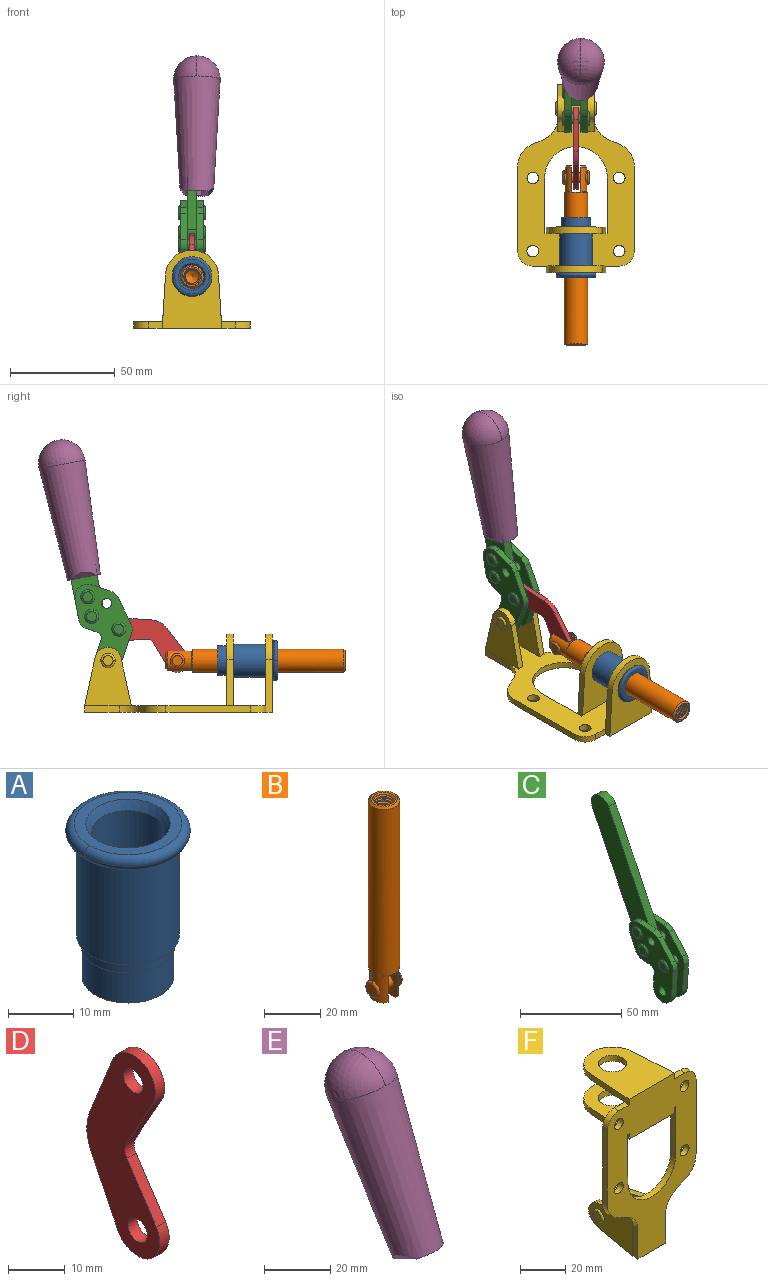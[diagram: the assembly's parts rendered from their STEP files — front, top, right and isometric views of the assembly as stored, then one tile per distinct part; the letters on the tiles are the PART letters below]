
ASSEMBLY  parts=6 mates=6
PART A: 15 faces, bbox 20.6x20.6x28.7 mm
  f0: torus R=8.26mm, axis (0,0,1), area 56.8mm2, adj f1,f10,f12
  f1: torus R=8.26mm, axis (0,0,1), area 56.8mm2, adj f0,f6,f13
  f2: cylinder r=5.59mm len=25.91mm, axis (0,0,1), area 909.6mm2, adj f3,f4
  f3: cone r=6.86mm half-angle=45deg, axis (0,0,-1), area 70.2mm2, adj f2,f14
  f4: cone r=6.47mm half-angle=30deg, axis (0,0,1), area 66.7mm2, adj f2,f13
  f5: cylinder r=7.04mm len=14.07mm, axis (0,0,1), area 252.6mm2, adj f11,f14
  f6: torus R=8.26mm, axis (0,0,1), area 56.8mm2, adj f1,f12,f13
  f7: cylinder r=7.16mm len=14.33mm, axis (0,0,1), area 91.5mm2, adj f9,f11
  f8: cylinder r=7.86mm len=18.42mm, axis (0,0,1), area 909.6mm2, adj f9,f10
  f9: plane 15.72x15.72mm, normal (0,0,-1), area 33mm2, adj f7,f8
  f10: plane 16.51x16.51mm, normal (0,0,-1), area 19.9mm2, adj f0,f8,f12
  f11: plane 14.33x14.33mm, normal (0,0,-1), area 5.7mm2, adj f5,f7
  f12: torus R=8.26mm, axis (0,0,1), area 56.8mm2, adj f0,f6,f10
  f13: plane 16.51x16.51mm, normal (0,0,1), area 82.7mm2, adj f1,f4,f6
  f14: plane 14.07x14.07mm, normal (0,0,-1), area 7.8mm2, adj f3,f5
PART B: 48 faces, bbox 12.6x11.1x86.1 mm
  f0: torus R=2.41mm, axis (-1,0,0), area 15mm2, adj f30,f32,f34
  f1: torus R=2.41mm, axis (-1,0,0), area 15mm2, adj f29,f31,f33
  f2: cylinder r=5.54mm len=72.39mm, axis (0,0,1), area 2518.5mm2, adj f3,f4,f42,f43
  f3: cone r=5.54mm half-angle=45deg, axis (0,0,1), area 7.6mm2, adj f2,f5,f41
  f4: cone r=5.54mm half-angle=45deg, axis (0,0,-1), area 34.9mm2, adj f2,f39
  f5: cylinder r=5.08mm len=11.48mm, axis (0,0,1), area 108.3mm2, adj f3,f7,f8,f41
  f6: cylinder r=2.41mm len=4.83mm, axis (-1,0,0), area 71.2mm2, adj f40,f41
  f7: cylinder r=2.41mm len=4.83mm, axis (-1,0,0), area 7.6mm2, adj f5,f34
  f8: cone r=5.08mm half-angle=45deg, axis (0,0,1), area 10.6mm2, adj f5,f37,f41
  f9: cone r=3.98mm half-angle=45deg, axis (0,0,1), area 17.6mm2, adj f27,f39,f45,f46,f47
  f10: cylinder r=2.41mm len=4.83mm, axis (-1,0,0), area 7.6mm2, adj f33,f38
  f11: cylinder r=3.2mm len=6.4mm, axis (0,0,1), area 78.4mm2, adj f12,f28,f44,f45,f47
  f12: cylinder r=3.2mm len=6.4mm, axis (0,0,1), area 10.5mm2, adj f11,f13,f45,f47
  f13: cylinder r=3.2mm len=6.4mm, axis (0,0,1), area 10.5mm2, adj f12,f14,f45,f47
  f14: cylinder r=3.2mm len=6.4mm, axis (0,0,1), area 10.5mm2, adj f13,f15,f45,f47
  f15: cylinder r=3.2mm len=6.4mm, axis (0,0,1), area 10.5mm2, adj f14,f16,f45,f47
  f16: cylinder r=3.2mm len=6.4mm, axis (0,0,1), area 10.5mm2, adj f15,f17,f45,f47
  f17: cylinder r=3.2mm len=6.4mm, axis (0,0,1), area 10.5mm2, adj f16,f18,f45,f47
  f18: cylinder r=3.2mm len=6.4mm, axis (0,0,1), area 10.5mm2, adj f17,f19,f45,f47
  f19: cylinder r=3.2mm len=6.4mm, axis (0,0,1), area 10.5mm2, adj f18,f20,f45,f47
  f20: cylinder r=3.2mm len=6.4mm, axis (0,0,1), area 10.5mm2, adj f19,f21,f45,f47
  f21: cylinder r=3.2mm len=6.4mm, axis (0,0,1), area 10.5mm2, adj f20,f22,f45,f47
  f22: cylinder r=3.2mm len=6.4mm, axis (0,0,1), area 10.5mm2, adj f21,f23,f45,f47
  f23: cylinder r=3.2mm len=6.4mm, axis (0,0,1), area 10.5mm2, adj f22,f24,f45,f47
  f24: cylinder r=3.2mm len=6.4mm, axis (0,0,1), area 10.5mm2, adj f23,f25,f45,f47
  f25: cylinder r=3.2mm len=6.4mm, axis (0,0,1), area 10.5mm2, adj f24,f26,f45,f47
  f26: cylinder r=3.2mm len=6.4mm, axis (0,0,1), area 10.5mm2, adj f25,f27,f45,f47
  f27: cylinder r=3.2mm len=6.4mm, axis (0,0,1), area 7.4mm2, adj f9,f26,f45,f47
  f28: cone r=3.2mm half-angle=60deg, axis (0,0,1), area 37.2mm2, adj f11
  f29: plane 4.83x4.83mm, normal (-1,0,0), area 18.3mm2, adj f1,f31
  f30: plane 4.83x4.83mm, normal (1,0,0), area 18.3mm2, adj f0,f32
  f31: torus R=2.41mm, axis (-1,0,0), area 15mm2, adj f1,f29,f33
  f32: torus R=2.41mm, axis (-1,0,0), area 15mm2, adj f0,f30,f34
  f33: plane 6.83x6.83mm, normal (1,0,0), area 18.3mm2, adj f1,f10,f31
  f34: plane 6.83x6.83mm, normal (-1,0,0), area 18.3mm2, adj f0,f7,f32
  f35: cone r=5.08mm half-angle=45deg, axis (0,0,1), area 10.6mm2, adj f36,f38,f40
  f36: plane 7.25x1.97mm, normal (0,0,-1), area 10mm2, adj f35,f40
  f37: plane 7.25x1.97mm, normal (0,0,-1), area 10mm2, adj f8,f41
  f38: cylinder r=5.08mm len=11.48mm, axis (0,0,1), area 108.3mm2, adj f10,f35,f40,f42
  f39: plane 9.55x9.55mm, normal (0,0,1), area 22mm2, adj f4,f9
  f40: plane 12.76x10.09mm, normal (1,0,0), area 95.7mm2, adj f6,f35,f36,f38,f42,f43
  f41: plane 12.76x10.09mm, normal (-1,0,0), area 95.7mm2, adj f3,f5,f6,f8,f37,f43
  f42: cone r=5.54mm half-angle=45deg, axis (0,0,1), area 7.6mm2, adj f2,f38,f40
  f43: plane 11.07x4.7mm, normal (0,0,-1), area 50.4mm2, adj f2,f40,f41
  f44: plane 0.89x0.62mm, normal (-1,0,0), area 0.3mm2, adj f11,f45,f46,f47
  f45: bspline ~24.8x7.63mm, area 266.6mm2, adj f9,f11,f12,f13,f14,f15,f16,f17
  f46: bspline ~24.87x7.63mm, area 73.6mm2, adj f9,f44,f45,f47
  f47: bspline ~24.98x7.63mm, area 272.5mm2, adj f9,f11,f12,f13,f14,f15,f16,f17
PART C: 59 faces, bbox 12.9x60.2x99.6 mm
  f0: torus R=2.39mm, axis (-1,0,0), area 14.9mm2, adj f20,f43,f51
  f1: torus R=2.39mm, axis (-1,0,0), area 14.9mm2, adj f19,f42,f51
  f2: torus R=2.39mm, axis (-1,0,0), area 14.9mm2, adj f18,f35,f51
  f3: torus R=2.39mm, axis (-1,0,0), area 14.9mm2, adj f14,f17,f23
  f4: torus R=2.39mm, axis (-1,0,0), area 14.9mm2, adj f13,f16,f23
  f5: torus R=2.39mm, axis (-1,0,0), area 14.9mm2, adj f12,f15,f23
  f6: cylinder r=2.39mm len=4.78mm, axis (1,0,0), area 46.5mm2, adj f48,f50,f51
  f7: cylinder r=2.39mm len=4.78mm, axis (1,0,0), area 46.5mm2, adj f50,f51
  f8: cylinder r=6.35mm len=12.68mm, axis (1,0,0), area 61.8mm2, adj f38,f39,f50,f51
  f9: cylinder r=2.39mm len=4.78mm, axis (-1,0,0), area 70.5mm2, adj f46,f50
  f10: cylinder r=2.39mm len=4.78mm, axis (-1,0,0), area 46.5mm2, adj f23,f45,f46
  f11: cylinder r=2.39mm len=4.78mm, axis (-1,0,0), area 46.5mm2, adj f23,f46
  f12: plane 4.78x4.78mm, normal (1,0,0), area 17.9mm2, adj f5,f15
  f13: plane 4.78x4.78mm, normal (1,0,0), area 17.9mm2, adj f4,f16
  f14: plane 4.78x4.78mm, normal (1,0,0), area 17.9mm2, adj f3,f17
  f15: torus R=2.39mm, axis (-1,0,0), area 14.9mm2, adj f5,f12,f23
  f16: torus R=2.39mm, axis (-1,0,0), area 14.9mm2, adj f4,f13,f23
  f17: torus R=2.39mm, axis (-1,0,0), area 14.9mm2, adj f3,f14,f23
  f18: plane 4.78x4.78mm, normal (-1,0,0), area 17.9mm2, adj f2,f35
  f19: plane 4.78x4.78mm, normal (-1,0,0), area 17.9mm2, adj f1,f42
  f20: plane 4.78x4.78mm, normal (-1,0,0), area 17.9mm2, adj f0,f43
  f21: plane 2.26x0.2mm, normal (1,0,0), area 0.2mm2, adj f31,f44
  f22: plane 2.26x0.2mm, normal (-1,0,0), area 0.2mm2, adj f41,f44
  f23: plane 39.37x30.77mm, normal (1,0,0), area 565.5mm2, adj f3,f4,f5,f10,f11,f15,f16,f17
  f24: cylinder r=6.1mm len=4.15mm, axis (-1,0,0), area 14.7mm2, adj f23,f25,f32,f46
  f25: plane 10.25x9.01mm, normal (0,-0.75,0.66), area 42.3mm2, adj f23,f24,f26,f46
  f26: cylinder r=6.35mm len=4.64mm, axis (-1,0,0), area 15.6mm2, adj f23,f25,f27,f46
  f27: plane 15.84x3.1mm, normal (0,-1,-0.07), area 49.2mm2, adj f23,f26,f28,f46
  f28: cylinder r=6.35mm len=12.68mm, axis (-1,0,0), area 61.8mm2, adj f23,f27,f29,f46
  f29: plane 8.11x3.1mm, normal (0,1,0.07), area 25.2mm2, adj f23,f28,f30,f46
  f30: cylinder r=3.05mm len=3.25mm, axis (-1,0,0), area 14.8mm2, adj f23,f29,f31,f46
  f31: plane 5.99x3.1mm, normal (0,0.07,-1), area 18.6mm2, adj f21,f23,f30,f44,f46
  f32: plane 9.5x3.1mm, normal (0,-0.07,1), area 29.5mm2, adj f23,f24,f33,f46,f47
  f33: cylinder r=6.1mm len=8.63mm, axis (-1,0,0), area 39.1mm2, adj f23,f32,f34,f47
  f34: plane 8.65x3.96mm, normal (0,0.91,-0.42), area 29.5mm2, adj f23,f33,f44,f47
  f35: torus R=2.39mm, axis (-1,0,0), area 14.9mm2, adj f2,f18,f51
  f36: plane 10.25x9.01mm, normal (0,-0.75,0.66), area 42.3mm2, adj f37,f49,f50,f51
  f37: cylinder r=6.35mm len=4.64mm, axis (1,0,0), area 15.6mm2, adj f36,f38,f50,f51
  f38: plane 15.84x3.1mm, normal (0,-1,-0.07), area 49.2mm2, adj f8,f37,f50,f51
  f39: plane 8.11x3.1mm, normal (0,1,0.07), area 25.2mm2, adj f8,f40,f50,f51
  f40: cylinder r=3.05mm len=3.25mm, axis (1,0,0), area 14.8mm2, adj f39,f41,f50,f51
  f41: plane 5.99x3.1mm, normal (0,0.07,-1), area 18.6mm2, adj f22,f40,f44,f50,f51
  f42: torus R=2.39mm, axis (-1,0,0), area 14.9mm2, adj f1,f19,f51
  f43: torus R=2.39mm, axis (-1,0,0), area 14.9mm2, adj f0,f20,f51
  f44: cylinder r=6.35mm len=12.12mm, axis (-1,0,0), area 128.9mm2, adj f21,f22,f23,f31,f34,f41,f46,f47
  f45: plane 2.65x1.35mm, normal (1,0,0), area 1mm2, adj f10,f55
  f46: plane 39.08x20.42mm, normal (-1,0,0), area 412.5mm2, adj f9,f10,f11,f24,f25,f26,f27,f28
  f47: plane 77.62x39.82mm, normal (1,0,0), area 850mm2, adj f32,f33,f34,f44,f53,f54,f55
  f48: plane 2.65x1.35mm, normal (-1,0,0), area 1mm2, adj f6,f55
  f49: cylinder r=6.1mm len=4.15mm, axis (1,0,0), area 14.7mm2, adj f36,f50,f51,f56
  f50: plane 39.08x20.42mm, normal (1,0,0), area 412.5mm2, adj f6,f7,f8,f9,f36,f37,f38,f39
  f51: plane 39.37x30.77mm, normal (-1,0,0), area 565.5mm2, adj f0,f1,f2,f6,f7,f8,f35,f36
  f52: plane 8.65x3.96mm, normal (0,0.91,-0.42), area 29.5mm2, adj f44,f51,f57,f58
  f53: plane 68.49x33.4mm, normal (0,0.9,-0.44), area 358.1mm2, adj f44,f47,f54,f58
  f54: cylinder r=6.35mm len=12.06mm, axis (1,0,0), area 93.7mm2, adj f47,f53,f55,f58
  f55: plane 68.49x33.4mm, normal (0,-0.9,0.44), area 358.1mm2, adj f44,f45,f46,f47,f48,f50,f54,f58
  f56: plane 9.5x3.1mm, normal (0,-0.07,1), area 29.5mm2, adj f49,f50,f51,f57,f58
  f57: cylinder r=6.1mm len=8.63mm, axis (1,0,0), area 39.1mm2, adj f51,f52,f56,f58
  f58: plane 77.62x39.82mm, normal (-1,0,0), area 850mm2, adj f44,f52,f53,f54,f55,f56,f57
PART D: 12 faces, bbox 2.3x18.2x42.8 mm
  f0: cylinder r=2.4mm len=4.8mm, axis (1,0,0), area 34.9mm2, adj f4,f11
  f1: cylinder r=10.41mm len=8.47mm, axis (1,0,0), area 20.2mm2, adj f4,f9,f10,f11
  f2: cylinder r=3.05mm len=3.16mm, axis (1,0,0), area 7.7mm2, adj f4,f6,f7,f11
  f3: cylinder r=2.4mm len=4.8mm, axis (1,0,0), area 34.9mm2, adj f4,f11
  f4: plane 42.81x18.23mm, normal (-1,0,0), area 414.1mm2, adj f0,f1,f2,f3,f5,f6,f7,f8
  f5: cylinder r=5.54mm len=10.67mm, axis (1,0,0), area 41.8mm2, adj f4,f6,f10,f11
  f6: plane 11.66x6.53mm, normal (0,-0.87,-0.49), area 30.9mm2, adj f2,f4,f5,f11
  f7: plane 11.17x7.33mm, normal (0,-0.84,0.55), area 30.9mm2, adj f2,f4,f8,f11
  f8: cylinder r=5.54mm len=10.51mm, axis (1,0,0), area 41.8mm2, adj f4,f7,f9,f11
  f9: plane 13.67x6.67mm, normal (0,0.9,-0.44), area 35.1mm2, adj f1,f4,f8,f11
  f10: plane 14.1x5.7mm, normal (0,0.93,0.37), area 35.1mm2, adj f1,f4,f5,f11
  f11: plane 42.81x18.23mm, normal (1,0,0), area 414.1mm2, adj f0,f1,f2,f3,f5,f6,f7,f8
PART E: 11 faces, bbox 22.3x42.6x64.5 mm
  f0: sphere r=11.13mm, area 411.4mm2, adj f1,f8
  f1: cone r=11.11mm half-angle=3.3deg, axis (0,0.44,0.9), area 3251.8mm2, adj f0,f7,f8,f9,f10
  f2: cylinder r=6.16mm len=11.7mm, axis (1,0,0), area 89.5mm2, adj f3,f4,f5,f6
  f3: plane 60.23x36.75mm, normal (-1,0,0), area 763.6mm2, adj f2,f4,f6,f10
  f4: plane 51.37x25.05mm, normal (0,0.9,-0.44), area 264.2mm2, adj f2,f3,f5,f10
  f5: plane 60.23x36.75mm, normal (1,0,0), area 763.6mm2, adj f2,f4,f6,f10
  f6: plane 51.37x25.05mm, normal (0,-0.9,0.44), area 264.2mm2, adj f2,f3,f5,f10
  f7: plane 9.95x5.95mm, normal (0.71,-0.31,-0.64), area 25.8mm2, adj f1,f10
  f8: sphere r=11.13mm, area 411.4mm2, adj f0,f1
  f9: plane 9.95x5.95mm, normal (-0.71,-0.31,-0.64), area 25.8mm2, adj f1,f10
  f10: plane 14.27x11.38mm, normal (0,-0.44,-0.9), area 106.7mm2, adj f1,f3,f4,f5,f6,f7,f9
PART F: 55 faces, bbox 55.7x37.4x89.8 mm
  f0: torus R=2.41mm, axis (-1,0,0), area 15mm2, adj f11,f15,f25
  f1: torus R=2.41mm, axis (-1,0,0), area 15mm2, adj f10,f12,f22
  f2: cylinder r=2.78mm len=5.56mm, axis (0,-1,0), area 54.2mm2, adj f30,f54
  f3: cylinder r=14.99mm len=29.97mm, axis (0,-1,0), area 145.9mm2, adj f30,f49,f53,f54
  f4: cylinder r=2.78mm len=5.56mm, axis (0,-1,0), area 54.2mm2, adj f30,f54
  f5: cylinder r=2.78mm len=5.56mm, axis (0,-1,0), area 54.2mm2, adj f30,f54
  f6: cylinder r=2.78mm len=5.56mm, axis (0,-1,0), area 54.2mm2, adj f30,f54
  f7: cylinder r=6.35mm len=12.7mm, axis (0,0,1), area 123.6mm2, adj f27,f51
  f8: cylinder r=6.35mm len=12.7mm, axis (0,0,-1), area 124.7mm2, adj f21,f35
  f9: cylinder r=2.41mm len=11.18mm, axis (-1,0,0), area 169.4mm2, adj f16,f19
  f10: plane 4.83x4.83mm, normal (1,0,0), area 18.3mm2, adj f1,f12
  f11: plane 4.83x4.83mm, normal (-1,0,0), area 18.3mm2, adj f0,f15
  f12: torus R=2.41mm, axis (-1,0,0), area 15mm2, adj f1,f10,f22
  f13: cylinder r=6.35mm len=12.41mm, axis (1,0,0), area 53.4mm2, adj f18,f19,f22,f23
  f14: cylinder r=6.35mm len=12.41mm, axis (-1,0,0), area 53.4mm2, adj f16,f17,f24,f25
  f15: torus R=2.41mm, axis (-1,0,0), area 15mm2, adj f0,f11,f25
  f16: plane 27.86x22.35mm, normal (1,0,0), area 425.4mm2, adj f9,f14,f17,f24,f30
  f17: plane 22.86x4.97mm, normal (0,0.21,0.98), area 72.5mm2, adj f14,f16,f25,f30
  f18: plane 22.86x4.97mm, normal (0,0.21,0.98), area 72.5mm2, adj f13,f19,f22,f30
  f19: plane 27.86x22.35mm, normal (-1,0,0), area 425.4mm2, adj f9,f13,f18,f23,f30
  f20: cylinder r=12.7mm len=25.35mm, axis (0,0,-1), area 119.8mm2, adj f21,f34,f35,f36
  f21: plane 34.21x28.07mm, normal (0,0,-1), area 702.4mm2, adj f8,f20,f30,f34,f36
  f22: plane 27.96x22.45mm, normal (1,0,0), area 407.2mm2, adj f1,f12,f13,f18,f23,f30,f42,f43
  f23: plane 22.86x4.97mm, normal (0,0.21,-0.98), area 72.5mm2, adj f13,f19,f22,f44
  f24: plane 22.86x4.97mm, normal (0,0.21,-0.98), area 72.5mm2, adj f14,f16,f25,f44
  f25: plane 27.86x22.35mm, normal (-1,0,0), area 407.1mm2, adj f0,f14,f15,f17,f24,f30,f45,f46
  f26: plane 3.1x0.95mm, normal (0,0,-1), area 2.7mm2, adj f30,f49,f50,f54
  f27: plane 34.21x28.07mm, normal (0,0,1), area 702.4mm2, adj f7,f28,f30,f50,f52
  f28: cylinder r=12.7mm len=25.35mm, axis (0,0,1), area 118.8mm2, adj f27,f50,f51,f52
  f29: plane 3.1x0.95mm, normal (0,0,-1), area 2.7mm2, adj f30,f52,f53,f54
  f30: plane 86.54x55.63mm, normal (0,1,0), area 2362.9mm2, adj f2,f3,f4,f5,f6,f16,f17,f18
  f31: plane 40.56x3.1mm, normal (-1,0,0), area 125.7mm2, adj f30,f32,f48,f54
  f32: cylinder r=7.11mm len=7.11mm, axis (0,-1,0), area 34.6mm2, adj f30,f31,f33,f54
  f33: plane 6.67x3.1mm, normal (0,0,1), area 20.4mm2, adj f30,f32,f34,f54
  f34: plane 25.39x3.13mm, normal (-1,0.06,0), area 79.5mm2, adj f20,f21,f33,f35,f54
  f35: plane 37.31x28.45mm, normal (0,0,1), area 789.9mm2, adj f8,f20,f34,f36,f54
  f36: plane 25.39x3.13mm, normal (1,0.06,0), area 79.5mm2, adj f20,f21,f35,f37,f54
  f37: plane 6.67x3.1mm, normal (0,0,1), area 20.4mm2, adj f30,f36,f38,f54
  f38: cylinder r=7.11mm len=7.11mm, axis (0,-1,0), area 34.6mm2, adj f30,f37,f39,f54
  f39: plane 40.56x3.1mm, normal (1,0,0), area 125.7mm2, adj f30,f38,f40,f54
  f40: cylinder r=11.18mm len=10.16mm, axis (0,-1,0), area 39.5mm2, adj f30,f39,f41,f54
  f41: plane 6.09x3.1mm, normal (0.42,0,-0.91), area 20.8mm2, adj f30,f40,f42,f54
  f42: cylinder r=11.18mm len=9.41mm, axis (0,-1,0), area 37.2mm2, adj f22,f30,f41,f43,f54
  f43: plane 16.5x3.1mm, normal (1,0,0), area 51.1mm2, adj f22,f42,f44,f54
  f44: plane 17.37x3.1mm, normal (0,0,-1), area 53.8mm2, adj f23,f24,f30,f43,f45,f54
  f45: plane 16.5x3.1mm, normal (-1,0,0), area 51.1mm2, adj f25,f44,f46,f54
  f46: cylinder r=11.18mm len=9.41mm, axis (0,-1,0), area 37.2mm2, adj f25,f30,f45,f47,f54
  f47: plane 6.09x3.1mm, normal (-0.42,0,-0.91), area 20.8mm2, adj f30,f46,f48,f54
  f48: cylinder r=11.18mm len=10.16mm, axis (0,-1,0), area 39.5mm2, adj f30,f31,f47,f54
  f49: plane 26.54x3.1mm, normal (-1,0,0), area 82.3mm2, adj f3,f26,f30,f54
  f50: plane 25.39x3.1mm, normal (1,0.06,0), area 78.8mm2, adj f26,f27,f28,f51,f54
  f51: plane 37.31x28.45mm, normal (0,0,-1), area 789.9mm2, adj f7,f28,f50,f52,f54
  f52: plane 25.39x3.1mm, normal (-1,0.06,0), area 78.8mm2, adj f27,f28,f29,f51,f54
  f53: plane 26.54x3.1mm, normal (1,0,0), area 82.3mm2, adj f3,f29,f30,f54
  f54: plane 89.66x55.63mm, normal (0,-1,0), area 2678.5mm2, adj f2,f3,f4,f5,f6,f26,f29,f31
PLACE A rot(axis=(1,0,0),90deg) t=(0,9.14,0)mm
PLACE B rot(axis=(1,0,0),90deg) t=(0,23.56,0)mm
PLACE C rot(axis=(1,0,0),15deg) t=(0,9.15,49.24)mm
PLACE D rot(axis=(0,-0.53,-0.85),180deg) t=(0,33.05,10.71)mm
PLACE E rot(axis=(1,0,0),15deg) t=(2.35,9.15,49.24)mm
PLACE F rot(axis=(1,0,0),90deg) t=(0,9.14,0)mm fixed
MATE revolute C.f7 <-> F.f0  axis (-1,0,0) through (0,41.23,24.61)mm
MATE revolute D.f5 <-> C.f4  axis (-1,0,0) through (0,36.06,39.62)mm
MATE fastened A.f2 <-> F.f7  axis (0,-1,0) through (0,-37.25,24.61)mm
MATE slider B.f2 <-> F.f7  axis (0,-1,0) through (0,-35.22,24.61)mm
MATE revolute D.f3 <-> B.f6  axis (-1,0,0) through (0,8.09,24.61)mm
MATE fastened C.f54 <-> E.f2  axis (1,0,0) through (2.35,63.6,120.54)mm
